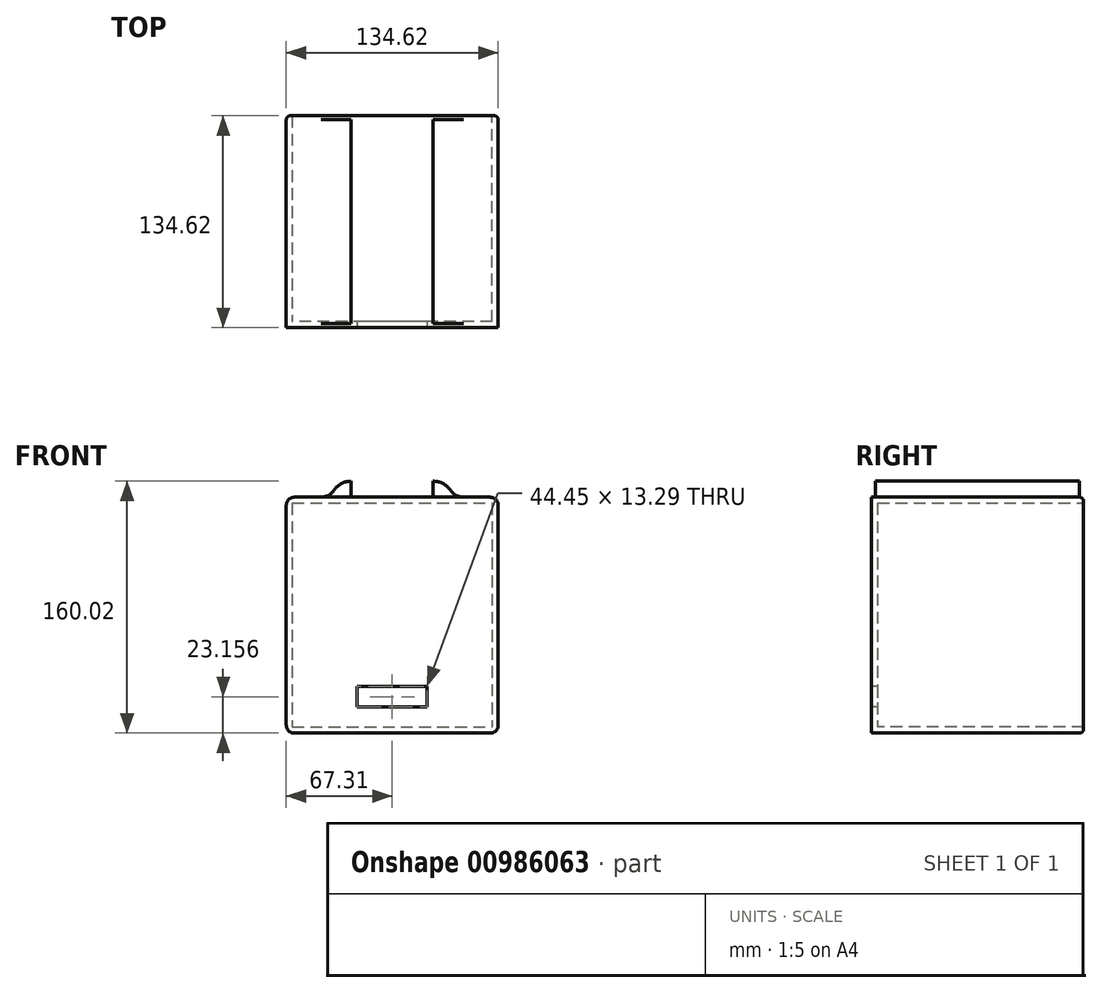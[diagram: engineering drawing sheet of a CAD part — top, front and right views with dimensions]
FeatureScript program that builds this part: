
annotation { "Feature Type Name" : "Feature", "Feature Type Description" : "" }
export const myFeature = defineFeature(function(context is Context, id is Id, definition is map)
    precondition{}
    {
        {
            var Q0;
            Q0=qCreatedBy(makeId("Top.planeOp"),FACE);
            var sketch = newSketch(context, id + "F0", { "sketchPlane" : qUnion([Q0])});
            skLineSegment(sketch, "E0.bottom", {"start": v(67.31, 67.3) * mm, "end": v(-67.3, 67.3) * mm});
            skLineSegment(sketch, "E0.top", {"start": v(67.3, -67.3) * mm, "end": v(-67.31, -67.3) * mm});
            skLineSegment(sketch, "E0.left", {"start": v(67.3, 67.3) * mm, "end": v(67.3, -67.31) * mm});
            skLineSegment(sketch, "E0.right", {"start": v(-67.3, 67.31) * mm, "end": v(-67.3, -67.3) * mm});
            skPoint(sketch, "E0.middle", {"position": v(0, 0) * mm});
            skLineSegment(sketch, "E1.bottom", {"start": v(63.5, 63.5) * mm, "end": v(-63.5, 63.5) * mm});
            skLineSegment(sketch, "E1.top", {"start": v(63.5, -63.5) * mm, "end": v(-63.5, -63.5) * mm});
            skLineSegment(sketch, "E1.left", {"start": v(63.5, 63.5) * mm, "end": v(63.5, -63.5) * mm});
            skLineSegment(sketch, "E1.right", {"start": v(-63.5, 63.5) * mm, "end": v(-63.5, -63.5) * mm});
            skSolve(sketch);
        }
        {
            var Q0;
            Q0=makeQuery(id+"F0.imprint","IMPRINT",FACE,{"disambiguationData":[TD([[makeQuery(id+"F0.imprint","IMPRINT",EDGE,{"derivedFrom":sQuery(id+"F0.wireOp",EDGE,"E0.bottom")}),1.0]])]});
            extrude(context, id + "F1", {"entities" : qUnion([Q0]), "depth" : 140.97 * mm, "offsetDistance" : 25.4 * mm});
        }
        {
            var Q0;
            Q0=makeQuery(id+"F1.opExtrude","CAP_FACE",FACE,{"disambiguationData":[OSD([sQuery(id+"F0.wireOp",EDGE,"E0.bottom"),sQuery(id+"F0.wireOp",EDGE,"E0.top"),sQuery(id+"F0.wireOp",EDGE,"E0.left"),sQuery(id+"F0.wireOp",EDGE,"E0.right"),sQuery(id+"F0.wireOp",EDGE,"E1.bottom"),sQuery(id+"F0.wireOp",EDGE,"E1.top"),sQuery(id+"F0.wireOp",EDGE,"E1.left"),sQuery(id+"F0.wireOp",EDGE,"E1.right")])],"isStart":false});
            var sketch = newSketch(context, id + "F2", { "sketchPlane" : qUnion([Q0])});
            skLineSegment(sketch, "E2.bottom", {"start": v(67.31, 67.3) * mm, "end": v(-67.31, 67.3) * mm});
            skLineSegment(sketch, "E2.top", {"start": v(67.31, -67.3) * mm, "end": v(-67.31, -67.3) * mm});
            skLineSegment(sketch, "E2.left", {"start": v(67.31, 67.3) * mm, "end": v(67.31, -67.3) * mm});
            skLineSegment(sketch, "E2.right", {"start": v(-67.31, 67.3) * mm, "end": v(-67.31, -67.3) * mm});
            skPoint(sketch, "E2.middle", {"position": v(0, 0) * mm});
            skSolve(sketch);
        }
        {
            var Q0;
            Q0=qSketchRegion(id+"F2",true);
            extrude(context, id + "F3", {"entities" : qUnion([Q0]), "operationType" : NewBodyOperationType.ADD, "depth" : 5.08 * mm, "offsetDistance" : 25.4 * mm});
        }
        {
            var Q0;
            Q0=makeQuery(id+"F3.boolean.opBoolean","MERGE",FACE,{"derivedFrom":[makeQuery(id+"F1.opExtrude","SWEPT_FACE",FACE,{"disambiguationData":[OSD([sQuery(id+"F0.wireOp",EDGE,"E0.top")])]}),makeQuery(id+"F3.opExtrude","SWEPT_FACE",FACE,{"disambiguationData":[OSD([sQuery(id+"F2.wireOp",EDGE,"E2.top")])]})]});
            var sketch = newSketch(context, id + "F4", { "sketchPlane" : qUnion([Q0])});
            skLineSegment(sketch, "E3.bottom", {"start": v(-22.23, 12.7) * mm, "end": v(22.22, 12.7) * mm});
            skLineSegment(sketch, "E3.top", {"start": v(-22.23, 26) * mm, "end": v(22.22, 26) * mm});
            skLineSegment(sketch, "E3.left", {"start": v(-22.23, 12.7) * mm, "end": v(-22.23, 26) * mm});
            skLineSegment(sketch, "E3.right", {"start": v(22.22, 12.7) * mm, "end": v(22.22, 26) * mm});
            skLineSegment(sketch, "E4", {"start": v(0, 0) * mm, "end": v(0, 146.05) * mm});
            skPoint(sketch, "E5", {"position": v(0, 12.7) * mm});
            skSolve(sketch);
        }
        {
            var Q0;
            {var subQ0=sQuery(id+"F4.wireOp",EDGE,"E3.right");Q0=makeQuery(id+"F4.imprint","IMPRINT",FACE,{"disambiguationData":[TD([[makeQuery(id+"F4.imprint","IMPRINT",EDGE,{"derivedFrom":subQ0}),1.0]])]});}
            var Q1;
            {var subQ0=sQuery(id+"F4.wireOp",EDGE,"E3.left");Q1=makeQuery(id+"F4.imprint","IMPRINT",FACE,{"disambiguationData":[TD([[makeQuery(id+"F4.imprint","IMPRINT",EDGE,{"derivedFrom":subQ0}),-1.0]])]});}
            extrude(context, id + "F5", {"entities" : qUnion([Q0, Q1]), "operationType" : NewBodyOperationType.REMOVE, "endBound" : BoundingType.UP_TO_NEXT, "oppositeDirection" : true, "depth" : 25.4 * mm, "offsetDistance" : 25.4 * mm});
        }
        {
            var Q0;
            Q0=makeQuery(id+"F1.opExtrude","CAP_FACE",FACE,{"disambiguationData":[OSD([sQuery(id+"F0.wireOp",EDGE,"E0.bottom"),sQuery(id+"F0.wireOp",EDGE,"E0.top"),sQuery(id+"F0.wireOp",EDGE,"E0.left"),sQuery(id+"F0.wireOp",EDGE,"E0.right"),sQuery(id+"F0.wireOp",EDGE,"E1.bottom"),sQuery(id+"F0.wireOp",EDGE,"E1.top"),sQuery(id+"F0.wireOp",EDGE,"E1.left"),sQuery(id+"F0.wireOp",EDGE,"E1.right")])],"isStart":true});
            var sketch = newSketch(context, id + "F6", { "sketchPlane" : qUnion([Q0])});
            skLineSegment(sketch, "E6.bottom", {"start": v(67.3, 67.31) * mm, "end": v(-67.3, 67.31) * mm});
            skLineSegment(sketch, "E6.top", {"start": v(67.3, -67.3) * mm, "end": v(-67.3, -67.3) * mm});
            skLineSegment(sketch, "E6.left", {"start": v(67.3, 67.31) * mm, "end": v(67.3, -67.31) * mm});
            skLineSegment(sketch, "E6.right", {"start": v(-67.3, 67.31) * mm, "end": v(-67.3, -67.31) * mm});
            skSolve(sketch);
        }
        {
            var Q0;
            Q0 = qSketchRegion(id + "F6", true);
            extrude(context, id + "F7", {"entities" : qUnion([Q0]), "operationType" : NewBodyOperationType.ADD, "depth" : 3.8 * mm, "offsetDistance" : 25.4 * mm});
        }
        {
            var Q0;
            Q0=makeQuery(id+"F7.boolean.opBoolean","MERGE",FACE,{"derivedFrom":[makeQuery(id+"F3.boolean.opBoolean","MERGE",FACE,{"derivedFrom":[makeQuery(id+"F1.opExtrude","SWEPT_FACE",FACE,{"disambiguationData":[OSD([sQuery(id+"F0.wireOp",EDGE,"E0.bottom")])]}),makeQuery(id+"F3.opExtrude","SWEPT_FACE",FACE,{"disambiguationData":[OSD([sQuery(id+"F2.wireOp",EDGE,"E2.bottom")])]})]}),makeQuery(id+"F7.opExtrude","SWEPT_FACE",FACE,{"disambiguationData":[OSD([sQuery(id+"F6.wireOp",EDGE,"E6.top")])]})]});
            var sketch = newSketch(context, id + "F8", { "sketchPlane" : qUnion([Q0])});
            skLineSegment(sketch, "E7.bottom", {"start": v(63.5, 142.24) * mm, "end": v(-63.5, 142.24) * mm});
            skLineSegment(sketch, "E7.top", {"start": v(63.5, 0) * mm, "end": v(-63.5, 0) * mm});
            skLineSegment(sketch, "E7.left", {"start": v(63.5, 142.24) * mm, "end": v(63.5, 0) * mm});
            skLineSegment(sketch, "E7.right", {"start": v(-63.5, 142.24) * mm, "end": v(-63.5, 0) * mm});
            skSolve(sketch);
        }
        {
            var Q0;
            Q0=makeQuery(id+"F8.imprint","IMPRINT",FACE,{"disambiguationData":[TD([[makeQuery(id+"F8.imprint","IMPRINT",EDGE,{"derivedFrom":sQuery(id+"F8.wireOp",EDGE,"E7.bottom")}),1.0]])]});
            extrude(context, id + "F9", {"entities" : qUnion([Q0]), "operationType" : NewBodyOperationType.REMOVE, "oppositeDirection" : true, "depth" : 3.8 * mm, "offsetDistance" : 25.4 * mm});
        }
        {
            var Q0;
            Q0=makeQuery(id+"F9.boolean.opBoolean","COPY",FACE,{"derivedFrom":makeQuery(id+"F9.opExtrude","CAP_FACE",FACE,{"disambiguationData":[OSD([sQuery(id+"F8.wireOp",EDGE,"E7.bottom"),sQuery(id+"F8.wireOp",EDGE,"E7.top"),sQuery(id+"F8.wireOp",EDGE,"E7.left"),sQuery(id+"F8.wireOp",EDGE,"E7.right")])],"isStart":false})});
            var sketch = newSketch(context, id + "F10", { "sketchPlane" : qUnion([Q0])});
            skLineSegment(sketch, "E8.bottom", {"start": v(-63.5, 142.24) * mm, "end": v(63.5, 142.24) * mm});
            skLineSegment(sketch, "E8.top", {"start": v(-63.5, 140.97) * mm, "end": v(63.5, 140.97) * mm});
            skLineSegment(sketch, "E8.left", {"start": v(-63.5, 142.24) * mm, "end": v(-63.5, 140.97) * mm});
            skLineSegment(sketch, "E8.right", {"start": v(63.5, 142.24) * mm, "end": v(63.5, 140.97) * mm});
            skSolve(sketch);
        }
        {
            var Q0;
            Q0=makeQuery(id+"F10.imprint","IMPRINT",FACE,{"disambiguationData":[TD([[makeQuery(id+"F10.imprint","IMPRINT",EDGE,{"derivedFrom":sQuery(id+"F10.wireOp",EDGE,"E8.bottom")}),1.0]])]});
            var Q1;
            Q1=makeQuery(id+"F1.opExtrude","SWEPT_FACE",FACE,{"disambiguationData":[OSD([sQuery(id+"F0.wireOp",EDGE,"E1.top")])]});
            extrude(context, id + "F11", {"entities" : qUnion([Q0]), "operationType" : NewBodyOperationType.REMOVE, "endBound" : BoundingType.UP_TO_SURFACE, "oppositeDirection" : true, "depth" : 25.4 * mm, "endBoundEntityFace" : qUnion([Q1]), "offsetDistance" : 25.4 * mm});
        }
        {
            var Q0;
            Q0=makeQuery(id+"F7.opExtrude","CAP_EDGE",EDGE,{"disambiguationData":[OSD([sQuery(id+"F6.wireOp",EDGE,"E6.right")])],"isStart":false});
            var Q1;
            Q1=makeQuery(id+"F7.opExtrude","CAP_EDGE",EDGE,{"disambiguationData":[OSD([sQuery(id+"F6.wireOp",EDGE,"E6.left")])],"isStart":false});
            var Q2;
            Q2=makeQuery(id+"F3.opExtrude","CAP_EDGE",EDGE,{"disambiguationData":[OSD([sQuery(id+"F2.wireOp",EDGE,"E2.left")])],"isStart":false});
            var Q3;
            Q3=makeQuery(id+"F3.opExtrude","CAP_EDGE",EDGE,{"disambiguationData":[OSD([sQuery(id+"F2.wireOp",EDGE,"E2.right")])],"isStart":false});
            fillet(context, id + "F12", {"entities" : qUnion([Q0, Q1, Q2, Q3]), "radius" : 5.08 * mm, "tangentPropagation" : true, "allowEdgeOverflow" : false});
        }
        {
            var Q0;
            Q0=makeQuery(id+"F7.boolean.opBoolean","MERGE",EDGE,{"derivedFrom":[makeQuery(id+"F3.boolean.opBoolean","MERGE",EDGE,{"derivedFrom":[makeQuery(id+"F1.opExtrude","SWEPT_EDGE",EDGE,{"disambiguationData":[OSD([sQuery(id+"F0.wireOp",EDGE,"E0.bottom"),sQuery(id+"F0.wireOp",EDGE,"E0.left")])]}),makeQuery(id+"F3.opExtrude","SWEPT_EDGE",EDGE,{"disambiguationData":[OSD([sQuery(id+"F2.wireOp",EDGE,"E2.bottom"),sQuery(id+"F2.wireOp",EDGE,"E2.left")])]})]}),makeQuery(id+"F7.opExtrude","SWEPT_EDGE",EDGE,{"disambiguationData":[OSD([sQuery(id+"F6.wireOp",EDGE,"E6.top"),sQuery(id+"F6.wireOp",EDGE,"E6.left")])]})]});
            var Q1;
            Q1=makeQuery(id+"F7.opExtrude","CAP_EDGE",EDGE,{"disambiguationData":[OSD([sQuery(id+"F6.wireOp",EDGE,"E6.top")])],"isStart":false});
            var Q2;
            Q2=makeQuery(id+"F3.opExtrude","CAP_EDGE",EDGE,{"disambiguationData":[OSD([sQuery(id+"F2.wireOp",EDGE,"E2.bottom")])],"isStart":false});
            var Q3;
            Q3=makeQuery(id+"F7.boolean.opBoolean","MERGE",EDGE,{"derivedFrom":[makeQuery(id+"F3.boolean.opBoolean","MERGE",EDGE,{"derivedFrom":[makeQuery(id+"F1.opExtrude","SWEPT_EDGE",EDGE,{"disambiguationData":[OSD([sQuery(id+"F0.wireOp",EDGE,"E0.bottom"),sQuery(id+"F0.wireOp",EDGE,"E0.right")])]}),makeQuery(id+"F3.opExtrude","SWEPT_EDGE",EDGE,{"disambiguationData":[OSD([sQuery(id+"F2.wireOp",EDGE,"E2.bottom"),sQuery(id+"F2.wireOp",EDGE,"E2.right")])]})]}),makeQuery(id+"F7.opExtrude","SWEPT_EDGE",EDGE,{"disambiguationData":[OSD([sQuery(id+"F6.wireOp",EDGE,"E6.top"),sQuery(id+"F6.wireOp",EDGE,"E6.right")])]})]});
            fillet(context, id + "F13", {"entities" : qUnion([Q0, Q1, Q2, Q3]), "radius" : 2.54 * mm, "tangentPropagation" : true, "allowEdgeOverflow" : false});
        }
        {
            var Q0;
            Q0=makeQuery(id+"F3.opExtrude","CAP_FACE",FACE,{"disambiguationData":[OSD([sQuery(id+"F2.wireOp",EDGE,"E2.bottom"),sQuery(id+"F2.wireOp",EDGE,"E2.top"),sQuery(id+"F2.wireOp",EDGE,"E2.left"),sQuery(id+"F2.wireOp",EDGE,"E2.right")])],"isStart":false});
            var sketch = newSketch(context, id + "F14", { "sketchPlane" : qUnion([Q0])});
            skLineSegment(sketch, "E9.bottom", {"start": v(26.04, 64.77) * mm, "end": v(-26.04, 64.77) * mm});
            skLineSegment(sketch, "E9.top", {"start": v(26.04, -64.77) * mm, "end": v(-26.04, -64.77) * mm});
            skLineSegment(sketch, "E9.left", {"start": v(26.04, 64.77) * mm, "end": v(26.04, -64.77) * mm});
            skLineSegment(sketch, "E9.right", {"start": v(-26.04, 64.77) * mm, "end": v(-26.04, -64.77) * mm});
            skPoint(sketch, "E9.middle", {"position": v(0, 0) * mm});
            skLineSegment(sketch, "E10.bottom", {"start": v(38.73, 64.77) * mm, "end": v(-38.73, 64.77) * mm});
            skLineSegment(sketch, "E10.top", {"start": v(38.73, -64.77) * mm, "end": v(-38.73, -64.77) * mm});
            skLineSegment(sketch, "E10.left", {"start": v(38.73, 64.77) * mm, "end": v(38.73, -64.77) * mm});
            skLineSegment(sketch, "E10.right", {"start": v(-38.73, 64.77) * mm, "end": v(-38.73, -64.77) * mm});
            skSolve(sketch);
        }
        {
            var Q0;
            {var subQ0=sQuery(id+"F14.wireOp",EDGE,"E9.right");Q0=makeQuery(id+"F14.imprint","IMPRINT",FACE,{"disambiguationData":[TD([[makeQuery(id+"F14.imprint","IMPRINT",EDGE,{"derivedFrom":subQ0}),-1.0]])]});}
            var Q1;
            {var subQ0=sQuery(id+"F14.wireOp",EDGE,"E9.left");Q1=makeQuery(id+"F14.imprint","IMPRINT",FACE,{"disambiguationData":[TD([[makeQuery(id+"F14.imprint","IMPRINT",EDGE,{"derivedFrom":subQ0}),1.0]])]});}
            extrude(context, id + "F15", {"entities" : qUnion([Q0, Q1]), "operationType" : NewBodyOperationType.ADD, "depth" : 10.16 * mm, "offsetDistance" : 25.4 * mm});
        }
        {
            var Q0;
            Q0=makeQuery(id+"F15.opExtrude","CAP_EDGE",EDGE,{"disambiguationData":[OSD([sQuery(id+"F14.wireOp",EDGE,"E10.right")])],"isStart":false});
            var Q1;
            Q1=makeQuery(id+"F15.opExtrude","CAP_EDGE",EDGE,{"disambiguationData":[OSD([sQuery(id+"F14.wireOp",EDGE,"E10.left")])],"isStart":false});
            fillet(context, id + "F16", {"entities" : qUnion([Q0, Q1]), "radius" : 12.7 * mm, "tangentPropagation" : true, "allowEdgeOverflow" : false});
        }
        {
            var Q0;
            Q0=makeQuery(id+"F16.opFillet","BLEND_EDGE",EDGE,{"blendedFrom":[makeQuery(id+"F15.opExtrude","CAP_EDGE",EDGE,{"disambiguationData":[OSD([sQuery(id+"F14.wireOp",EDGE,"E10.right")])],"isStart":false}),makeQuery(id+"F3.opExtrude","CAP_FACE",FACE,{"disambiguationData":[OSD([sQuery(id+"F2.wireOp",EDGE,"E2.bottom"),sQuery(id+"F2.wireOp",EDGE,"E2.top"),sQuery(id+"F2.wireOp",EDGE,"E2.left"),sQuery(id+"F2.wireOp",EDGE,"E2.right")])],"isStart":false})],"blendedInto":[makeQuery(id+"F3.opExtrude","CAP_FACE",FACE,{"disambiguationData":[OSD([sQuery(id+"F2.wireOp",EDGE,"E2.bottom"),sQuery(id+"F2.wireOp",EDGE,"E2.top"),sQuery(id+"F2.wireOp",EDGE,"E2.left"),sQuery(id+"F2.wireOp",EDGE,"E2.right")])],"isStart":false})]});
            var Q1;
            Q1=makeQuery(id+"F16.opFillet","BLEND_EDGE",EDGE,{"blendedFrom":[makeQuery(id+"F15.opExtrude","CAP_EDGE",EDGE,{"disambiguationData":[OSD([sQuery(id+"F14.wireOp",EDGE,"E10.left")])],"isStart":false}),makeQuery(id+"F3.opExtrude","CAP_FACE",FACE,{"disambiguationData":[OSD([sQuery(id+"F2.wireOp",EDGE,"E2.bottom"),sQuery(id+"F2.wireOp",EDGE,"E2.top"),sQuery(id+"F2.wireOp",EDGE,"E2.left"),sQuery(id+"F2.wireOp",EDGE,"E2.right")])],"isStart":false})],"blendedInto":[makeQuery(id+"F3.opExtrude","CAP_FACE",FACE,{"disambiguationData":[OSD([sQuery(id+"F2.wireOp",EDGE,"E2.bottom"),sQuery(id+"F2.wireOp",EDGE,"E2.top"),sQuery(id+"F2.wireOp",EDGE,"E2.left"),sQuery(id+"F2.wireOp",EDGE,"E2.right")])],"isStart":false})]});
            fillet(context, id + "F17", {"entities" : qUnion([Q0, Q1]), "radius" : 10.16 * mm, "tangentPropagation" : true, "allowEdgeOverflow" : false});
        }
    });
